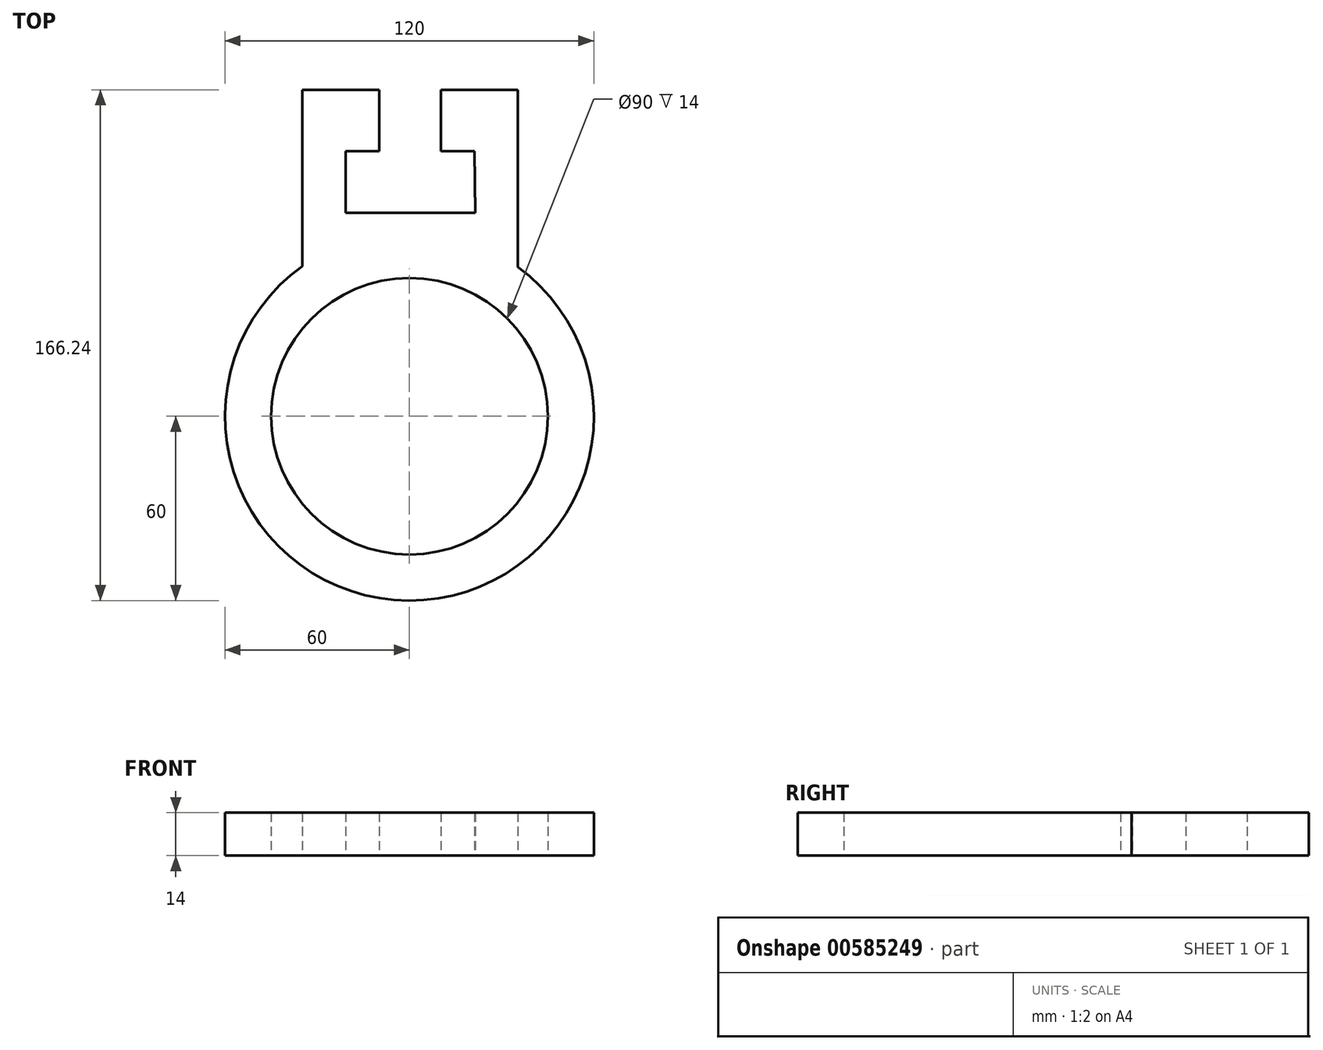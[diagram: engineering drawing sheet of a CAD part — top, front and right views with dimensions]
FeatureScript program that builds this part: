
annotation { "Feature Type Name" : "Feature", "Feature Type Description" : "" }
export const myFeature = defineFeature(function(context is Context, id is Id, definition is map)
    precondition{}
    {
        {
            var Q0;
            Q0=qCreatedBy(makeId("Top.planeOp"),FACE);
            var sketch = newSketch(context, id + "F0", { "sketchPlane" : qUnion([Q0])});
            skCircle(sketch, "E0", {"center": v(0, 0) * mm, "radius": 60 * mm});
            skCircle(sketch, "E1", {"center": v(0, 0) * mm, "radius": 45 * mm});
            skLineSegment(sketch, "E2.bottom", {"start": v(-34.8, 66.24) * mm, "end": v(35.2, 66.24) * mm});
            skLineSegment(sketch, "E2.top", {"start": v(-34.8, 48.6) * mm, "end": v(35.2, 48.6) * mm});
            skLineSegment(sketch, "E2.left", {"start": v(-34.8, 66.24) * mm, "end": v(-34.8, 48.6) * mm});
            skLineSegment(sketch, "E2.right", {"start": v(35.2, 66.24) * mm, "end": v(35.2, 48.6) * mm});
            skLineSegment(sketch, "E3", {"start": v(-34.8, 66.24) * mm, "end": v(-34.8, 106.24) * mm});
            skLineSegment(sketch, "E4", {"start": v(35.2, 66.24) * mm, "end": v(35.2, 106.24) * mm});
            skLineSegment(sketch, "E5", {"start": v(-34.8, 106.24) * mm, "end": v(-9.8, 106.24) * mm});
            skLineSegment(sketch, "E6", {"start": v(35.2, 106.24) * mm, "end": v(10.2, 106.24) * mm});
            skLineSegment(sketch, "E7", {"start": v(-9.8, 86.24) * mm, "end": v(-9.8, 106.24) * mm});
            skLineSegment(sketch, "E8", {"start": v(10.2, 106.24) * mm, "end": v(10.2, 86.24) * mm});
            skLineSegment(sketch, "E9", {"start": v(-9.8, 86.24) * mm, "end": v(-20.8, 86.24) * mm});
            skLineSegment(sketch, "E10", {"start": v(10.2, 86.24) * mm, "end": v(21.2, 86.24) * mm});
            skLineSegment(sketch, "E11", {"start": v(-20.8, 86.24) * mm, "end": v(-20.8, 66.24) * mm});
            skLineSegment(sketch, "E12", {"start": v(-20.8, 66.24) * mm, "end": v(21.4, 66.24) * mm});
            skLineSegment(sketch, "E13", {"start": v(21.2, 86.24) * mm, "end": v(21.4, 66.24) * mm});
            skSolve(sketch);
        }
        {
            var Q0;
            Q0 = qSketchRegion(id + "F0", true);
            extrude(context, id + "F1", {"entities" : qUnion([Q0]), "depth" : 14 * mm, "offsetDistance" : 25.4 * mm});
        }
    });
